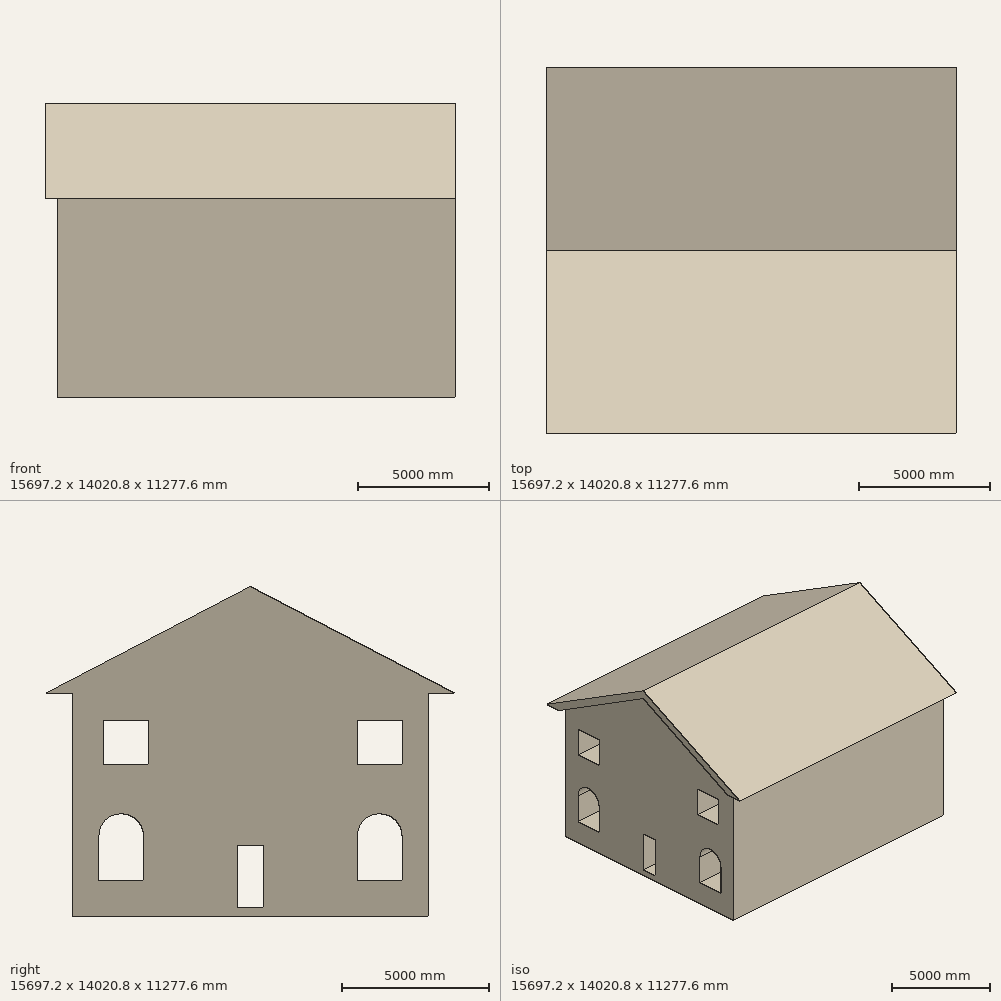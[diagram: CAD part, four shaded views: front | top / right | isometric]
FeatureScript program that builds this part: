
annotation { "Feature Type Name" : "Feature", "Feature Type Description" : "" }
export const myFeature = defineFeature(function(context is Context, id is Id, definition is map)
    precondition{}
    {
        {
            var Q0;
            Q0=qCreatedBy(makeId("Right.planeOp"),FACE);
            var sketch = newSketch(context, id + "F0", { "sketchPlane" : qUnion([Q0])});
            skLineSegment(sketch, "E0", {"start": v(0, 0) * mm, "end": v(-6096, 0) * mm});
            skLineSegment(sketch, "E1", {"start": v(0, 0) * mm, "end": v(6096, 0) * mm});
            skLineSegment(sketch, "E2", {"start": v(0, 3200.4) * mm, "end": v(6096, 0) * mm});
            skLineSegment(sketch, "E3", {"start": v(-6096, 0) * mm, "end": v(-6096, -7315.2) * mm});
            skLineSegment(sketch, "E4", {"start": v(0, 3200.4) * mm, "end": v(-6096, 0) * mm});
            skLineSegment(sketch, "E5", {"start": v(-6096, -7315.2) * mm, "end": v(6096, -7315.2) * mm});
            skLineSegment(sketch, "E6", {"start": v(6096, -7315.2) * mm, "end": v(6096, 0) * mm});
            skLineSegment(sketch, "E7", {"start": v(-6096, -7315.2) * mm, "end": v(-6096, -7620) * mm});
            skLineSegment(sketch, "E8", {"start": v(-6096, -7620) * mm, "end": v(6096, -7620) * mm});
            skLineSegment(sketch, "E9", {"start": v(6096, -7620) * mm, "end": v(6096, -7315.2) * mm});
            skLineSegment(sketch, "E10", {"start": v(0, 3200.4) * mm, "end": v(0, 0) * mm});
            skLineSegment(sketch, "E11", {"start": v(0, -7315.2) * mm, "end": v(-457.2, -7315.2) * mm});
            skLineSegment(sketch, "E12", {"start": v(-457.2, -7315.2) * mm, "end": v(-457.2, -5181.6) * mm});
            skLineSegment(sketch, "E13", {"start": v(-457.2, -5181.6) * mm, "end": v(457.2, -5181.6) * mm});
            skLineSegment(sketch, "E14", {"start": v(457.2, -5181.6) * mm, "end": v(457.2, -7315.2) * mm});
            skLineSegment(sketch, "E15", {"start": v(0, 3200.4) * mm, "end": v(0, 3657.6) * mm});
            skLineSegment(sketch, "E16", {"start": v(-6096, 0) * mm, "end": v(-7010.4, 0) * mm});
            skLineSegment(sketch, "E17", {"start": v(6096, 0) * mm, "end": v(7010.4, 0) * mm});
            skLineSegment(sketch, "E18", {"start": v(7010.4, 0) * mm, "end": v(0, 3657.6) * mm});
            skLineSegment(sketch, "E19", {"start": v(-7010.4, 0) * mm, "end": v(0, 3657.6) * mm});
            skLineSegment(sketch, "E20.bottom", {"start": v(-5016.97, -914.4) * mm, "end": v(-3492.97, -914.4) * mm});
            skLineSegment(sketch, "E20.top", {"start": v(-5016.97, -2438.4) * mm, "end": v(-3492.97, -2438.4) * mm});
            skLineSegment(sketch, "E20.left", {"start": v(-5016.97, -914.4) * mm, "end": v(-5016.97, -2438.4) * mm});
            skLineSegment(sketch, "E20.right", {"start": v(-3492.97, -914.4) * mm, "end": v(-3492.97, -2438.4) * mm});
            skLineSegment(sketch, "E21.bottom", {"start": v(3657.6, -914.4) * mm, "end": v(5181.6, -914.4) * mm});
            skLineSegment(sketch, "E21.top", {"start": v(3657.6, -2438.4) * mm, "end": v(5181.6, -2438.4) * mm});
            skLineSegment(sketch, "E21.left", {"start": v(3657.6, -914.4) * mm, "end": v(3657.6, -2438.4) * mm});
            skLineSegment(sketch, "E21.right", {"start": v(5181.6, -914.4) * mm, "end": v(5181.6, -2438.4) * mm});
            skLineSegment(sketch, "E22.bottom", {"start": v(-5181.6, -4876.8) * mm, "end": v(-3657.6, -4876.8) * mm});
            skLineSegment(sketch, "E22.top", {"start": v(-5181.6, -6400.8) * mm, "end": v(-3657.6, -6400.8) * mm});
            skLineSegment(sketch, "E22.left", {"start": v(-5181.6, -4876.8) * mm, "end": v(-5181.6, -6400.8) * mm});
            skLineSegment(sketch, "E22.right", {"start": v(-3657.6, -4876.8) * mm, "end": v(-3657.6, -6400.8) * mm});
            skArc(sketch, "E23", {"start": v(-3657.6, -4876.8) * mm, "mid": v(-4419.6, -4114.8) * mm, "end": v(-5181.6, -4876.8) * mm});
            skLineSegment(sketch, "E24.bottom", {"start": v(3657.6, -4876.8) * mm, "end": v(5181.6, -4876.8) * mm});
            skLineSegment(sketch, "E24.top", {"start": v(3657.6, -6400.8) * mm, "end": v(5181.6, -6400.8) * mm});
            skLineSegment(sketch, "E24.left", {"start": v(3657.6, -4876.8) * mm, "end": v(3657.6, -6400.8) * mm});
            skLineSegment(sketch, "E24.right", {"start": v(5181.6, -4876.8) * mm, "end": v(5181.6, -6400.8) * mm});
            skArc(sketch, "E25", {"start": v(5181.6, -4876.8) * mm, "mid": v(4419.6, -4114.8) * mm, "end": v(3657.6, -4876.8) * mm});
            skSolve(sketch);
        }
        {
            var Q0;
            {var subQ0=sQuery(id+"F0.wireOp",EDGE,"E7");Q0=makeQuery(id+"F0.imprint","IMPRINT",FACE,{"disambiguationData":[TD([[makeQuery(id+"F0.imprint","IMPRINT",EDGE,{"derivedFrom":subQ0}),1.0]])]});}
            var Q1;
            Q1=makeQuery(id+"F0.imprint","IMPRINT",FACE,{"disambiguationData":[TD([[makeQuery(id+"F0.imprint","IMPRINT",EDGE,{"derivedFrom":sQuery(id+"F0.wireOp",EDGE,"E4")}),-1.0]])]});
            var Q2;
            Q2=makeQuery(id+"F0.imprint","IMPRINT",FACE,{"disambiguationData":[TD([[makeQuery(id+"F0.imprint","IMPRINT",EDGE,{"derivedFrom":sQuery(id+"F0.wireOp",EDGE,"E1")}),1.0]])]});
            var Q3;
            Q3=makeQuery(id+"F0.imprint","IMPRINT",FACE,{"disambiguationData":[TD([[makeQuery(id+"F0.imprint","IMPRINT",EDGE,{"derivedFrom":sQuery(id+"F0.wireOp",EDGE,"E0")}),-1.0]])]});
            var Q4;
            {var subQ0=sQuery(id+"F0.wireOp",EDGE,"E11");Q4=makeQuery(id+"F0.imprint","IMPRINT",FACE,{"disambiguationData":[TD([[makeQuery(id+"F0.imprint","IMPRINT",EDGE,{"derivedFrom":subQ0}),-1.0]])]});}
            var Q5;
            Q5=makeQuery(id+"F0.imprint","IMPRINT",FACE,{"disambiguationData":[TD([[makeQuery(id+"F0.imprint","IMPRINT",EDGE,{"derivedFrom":sQuery(id+"F0.wireOp",EDGE,"E2")}),1.0]])]});
            var Q6;
            Q6=makeQuery(id+"F0.imprint","IMPRINT",FACE,{"disambiguationData":[TD([[makeQuery(id+"F0.imprint","IMPRINT",EDGE,{"derivedFrom":sQuery(id+"F0.wireOp",EDGE,"E0")}),1.0]])]});
            extrude(context, id + "F1", {"entities" : qUnion([Q0, Q1, Q2, Q3, Q4, Q5, Q6]), "depth" : 15240 * mm, "offsetDistance" : 30.48 * mm});
        }
        {
            var Q0;
            Q0=makeQuery(id+"F0.imprint","IMPRINT",FACE,{"disambiguationData":[TD([[makeQuery(id+"F0.imprint","IMPRINT",EDGE,{"derivedFrom":sQuery(id+"F0.wireOp",EDGE,"E2")}),1.0]])]});
            var Q1;
            Q1=makeQuery(id+"F0.imprint","IMPRINT",FACE,{"disambiguationData":[TD([[makeQuery(id+"F0.imprint","IMPRINT",EDGE,{"derivedFrom":sQuery(id+"F0.wireOp",EDGE,"E4")}),-1.0]])]});
            extrude(context, id + "F2", {"entities" : qUnion([Q0, Q1]), "operationType" : NewBodyOperationType.ADD, "endBound" : BoundingType.SYMMETRIC, "oppositeDirection" : true, "depth" : 914.4 * mm, "offsetDistance" : 30.48 * mm});
        }
    });
